# Revit family: Auto-Door_Sliding_BiPart_Wall_Tormax_TX9500
name_source: partatom
category: Doors
units: mm (PartAtom-declared; Revit-internal decimal feet)

## family parameters
Always vertical = Yes
Cut with Voids When Loaded = No
Host = Wall
OmniClass Number = 23.30.10.17.11
OmniClass Title = Sliding Doors
Room Calculation Point = No
Shared = No

## types (4) — shared parameters
Air Space Below Door = 0' - 0 5/16"
Analytic Construction = <None>
Assembly Code = B2030110
Available Options = [Standard Weatherstripping][Electric Lock][Battery Backup][Door Position Monitoring][I/O Module][Key Switch]
Construction Details = http://www.arcat.com
Define Thermal Properties by = Schematic Type
Fire Rating = as Specified
Frame Thickness = 0' - 4 1/2"
Glazing Thickness_Fixed Panel = 0' - 0 1/2"
Glazing Thickness_Sliding Panel = 0' - 0 1/2"
Green Building-LEED = http://www.arcat.com
Has Partial Breakout Capability = Yes
Keynote = 08463
Manufacturer = TORMAX USA Inc.
Manufacturer Fax = 210-494-5930
Manufacturer Website = http://www.tormaxusa.com
Max Height = 0' - 0"
Max Width = 0' - 0"
Miami Dade Conformance = Does Not Apply
Operating Temperature Range = Ambient -30F to 130F
Panel Thickness = 0' - 1 3/4"
Product Data = http://www.arcat.com
RO Spacing_Sides = 0' - 0 1/4"
RO Spacing_Top = 0' - 0 1/4"
Sales Information = http://www.tormaxusa.com
Send Message = http://www.arcat.com
Specification = http://www.arcat.com
Standards Conformance = ANSI A156.10  ;  NFPA 101  ;  UL325  ;  C-UL
Thickness = 0' - 1 3/4"
URL = http://www.tormaxusa.com
Wall Closure = By host
Water Penetration = as Specified
zero-valued in all types: Expected Lifespan (Years), Maintenance Schedule (Months), Warranty Duration (Years)

## per-type parameters (varying)
| type | Description | HD Drive | Height | Include Transom | Model | Transom Height | headerdepth |
| HD Glass Sidelight with no Transom | Tormax HD Automatic Sliding BiPart Door - All Glass TX9500HD as Specified | Yes | 7' - 8" | No | TX9500HD as Specified | 0' - 0" | 0' - 9 1/2" |
| HD Glass Sidelight with Transom | Tormax HD Automatic Sliding BiPart Door - All Glass TX9500HD as Specified | Yes | 11' - 0" | Yes | TX9500HD as Specified | 3' - 4" | 0' - 9 1/2" |
| Glass Sidelight with no Transom | Tormax Automatic Sliding BiPart Door - All Glass TX9500 as Specified | No | 7' - 8" | No | TX9500 as Specified | 0' - 0" | 0' - 8" |
| Glass Sidelight with Transom | Tormax Automatic Sliding BiPart Door - All Glass TX9500 as Specified | No | 11' - 0" | Yes | TX9500 as Specified | 3' - 4" | 0' - 8" |

## geometry (parser evidence)
native form markers: Sweep x8
no freeform markers — native parametric forms only
